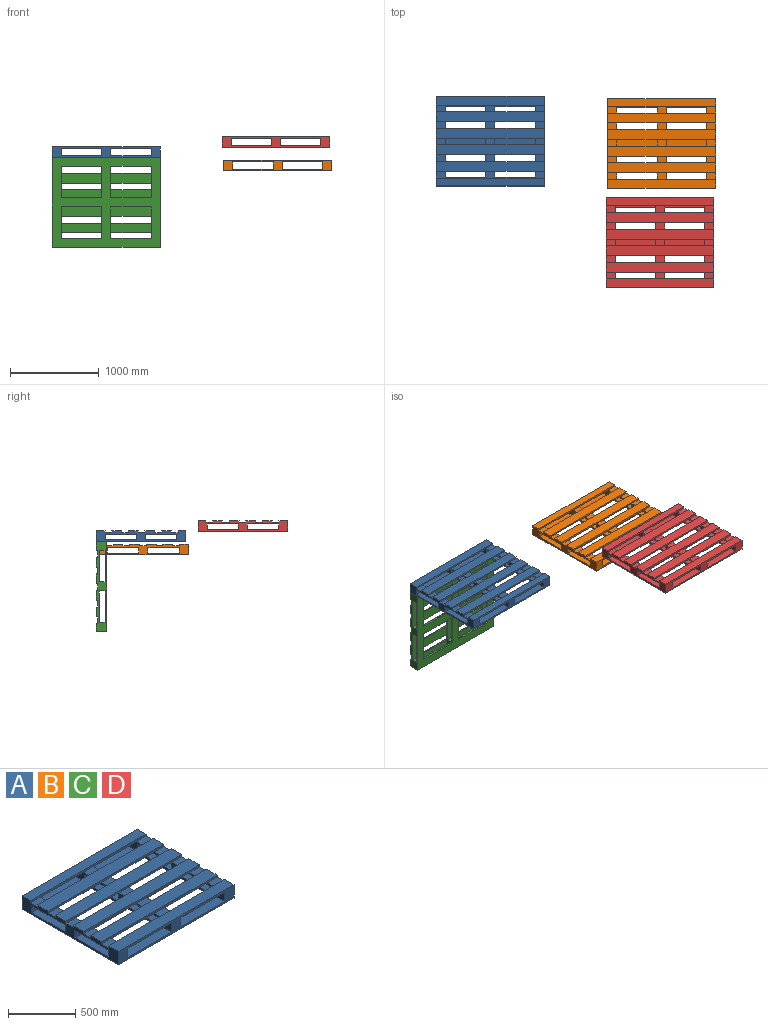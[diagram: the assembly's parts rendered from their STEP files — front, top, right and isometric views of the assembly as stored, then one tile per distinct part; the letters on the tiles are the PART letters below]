
ASSEMBLY  parts=4 mates=1
PART A: 98 faces, bbox 1219.2x1016x120.7 mm
  f0: plane 457.2x111.25mm, normal (0,0,-1), area 50864.4mm2, adj f36,f37,f88,f97
  f1: plane 457.2x111.25mm, normal (0,0,-1), area 50864.4mm2, adj f36,f37,f83,f92
  f2: plane 457.2x88.39mm, normal (0,0,-1), area 40412.8mm2, adj f23,f36,f37,f87
  f3: plane 457.2x111.25mm, normal (0,0,-1), area 50864.4mm2, adj f36,f37,f73,f78
  f4: plane 457.2x111.25mm, normal (0,0,-1), area 50864.4mm2, adj f36,f37,f77,f93
  f5: plane 457.2x111.25mm, normal (0,0,-1), area 50864.4mm2, adj f38,f40,f88,f97
  f6: plane 457.2x111.25mm, normal (0,0,-1), area 50864.4mm2, adj f38,f40,f83,f92
  f7: plane 457.2x88.39mm, normal (0,0,-1), area 40412.8mm2, adj f23,f38,f40,f87
  f8: plane 457.2x111.25mm, normal (0,0,-1), area 50864.4mm2, adj f38,f40,f73,f78
  f9: plane 457.2x111.25mm, normal (0,0,-1), area 50864.4mm2, adj f38,f40,f77,f93
  f10: plane 1219.2x111.25mm, normal (0,0,1), area 135638.4mm2, adj f15,f16,f88,f97
  f11: plane 1219.2x111.25mm, normal (0,0,1), area 135638.4mm2, adj f15,f16,f83,f92
  f12: plane 1219.2x88.39mm, normal (0,0,1), area 107767.5mm2, adj f15,f16,f23,f87
  f13: plane 1219.2x111.25mm, normal (0,0,1), area 135638.4mm2, adj f15,f16,f73,f78
  f14: plane 1219.2x111.25mm, normal (0,0,1), area 135638.4mm2, adj f15,f16,f77,f93
  f15: plane 1016x120.65mm, normal (1,0,0), area 70161.2mm2, adj f10,f11,f12,f13,f14,f17,f20,f23
  f16: plane 1016x120.65mm, normal (-1,0,0), area 70161.2mm2, adj f10,f11,f12,f13,f14,f17,f21,f22
  f17: plane 1219.2x120.65mm, normal (0,-1,0), area 71612.8mm2, adj f15,f16,f24,f27,f34,f36,f37,f38
  f18: plane 355.6x101.6mm, normal (0,0,-1), area 36129mm2, adj f36,f38,f48,f49
  f19: plane 355.6x101.6mm, normal (0,0,-1), area 36129mm2, adj f36,f38,f46,f47
  f20: plane 355.6x101.6mm, normal (0,0,-1), area 36129mm2, adj f15,f40,f44,f45
  f21: plane 355.6x101.6mm, normal (0,0,-1), area 36129mm2, adj f16,f37,f52,f53
  f22: plane 355.6x101.6mm, normal (0,0,-1), area 36129mm2, adj f16,f37,f50,f51
  f23: plane 1219.2x120.65mm, normal (0,1,0), area 71612.8mm2, adj f2,f7,f12,f15,f16,f24,f29,f33
  f24: plane 1219.2x1016mm, normal (0,0,-1), area 588385.9mm2, adj f15,f16,f17,f23,f54,f55,f56,f57
  f25: plane 457.2x101.6mm, normal (0,0,1), area 46451.5mm2, adj f38,f40,f59,f66
  f26: plane 355.6x101.6mm, normal (0,0,1), area 36129mm2, adj f15,f42,f43,f67
  f27: plane 457.2x101.6mm, normal (0,0,1), area 46451.5mm2, adj f17,f38,f40,f68
  f28: plane 355.6x101.6mm, normal (0,0,1), area 36129mm2, adj f16,f52,f53,f62
  f29: plane 457.2x101.6mm, normal (0,0,1), area 46451.5mm2, adj f23,f36,f37,f63
  f30: plane 457.2x101.6mm, normal (0,0,1), area 46451.5mm2, adj f36,f37,f56,f65
  f31: plane 355.6x101.6mm, normal (0,0,1), area 36129mm2, adj f15,f44,f45,f58
  f32: plane 355.6x101.6mm, normal (0,0,1), area 36129mm2, adj f48,f49,f60,f64
  f33: plane 457.2x101.6mm, normal (0,0,1), area 46451.5mm2, adj f23,f38,f40,f61
  f34: plane 457.2x101.6mm, normal (0,0,1), area 46451.5mm2, adj f17,f36,f37,f54
  f35: plane 355.6x101.6mm, normal (0,0,1), area 36129mm2, adj f16,f50,f51,f55
  f36: plane 1016x82.55mm, normal (-1,0,0), area 38709.6mm2, adj f0,f1,f2,f3,f4,f17,f18,f19
  f37: plane 1016x82.55mm, normal (1,0,0), area 38709.6mm2, adj f0,f1,f2,f3,f4,f17,f21,f22
  f38: plane 1016x82.55mm, normal (1,0,0), area 38709.6mm2, adj f5,f6,f7,f8,f9,f17,f18,f19
  f39: plane 355.6x101.6mm, normal (0,0,1), area 36129mm2, adj f46,f47,f57,f69
  f40: plane 1016x82.55mm, normal (-1,0,0), area 38709.6mm2, adj f5,f6,f7,f8,f9,f17,f20,f23
  f41: plane 355.6x101.6mm, normal (0,0,-1), area 36129mm2, adj f15,f40,f42,f43
  f42: plane 101.6x63.5mm, normal (0,1,0), area 6451.6mm2, adj f15,f26,f40,f41
  f43: plane 101.6x63.5mm, normal (0,-1,0), area 6451.6mm2, adj f15,f26,f40,f41
  f44: plane 101.6x63.5mm, normal (0,1,0), area 6451.6mm2, adj f15,f20,f31,f40
  f45: plane 101.6x63.5mm, normal (0,-1,0), area 6451.6mm2, adj f15,f20,f31,f40
  f46: plane 101.6x63.5mm, normal (0,1,0), area 6451.6mm2, adj f19,f36,f38,f39
  f47: plane 101.6x63.5mm, normal (0,-1,0), area 6451.6mm2, adj f19,f36,f38,f39
  f48: plane 101.6x63.5mm, normal (0,1,0), area 6451.6mm2, adj f18,f32,f36,f38
  f49: plane 101.6x63.5mm, normal (0,-1,0), area 6451.6mm2, adj f18,f32,f36,f38
  f50: plane 101.6x63.5mm, normal (0,1,0), area 6451.6mm2, adj f16,f22,f35,f37
  f51: plane 101.6x63.5mm, normal (0,-1,0), area 6451.6mm2, adj f16,f22,f35,f37
  f52: plane 101.6x63.5mm, normal (0,-1,0), area 6451.6mm2, adj f16,f21,f28,f37
  f53: plane 101.6x63.5mm, normal (0,1,0), area 6451.6mm2, adj f16,f21,f28,f37
  f54: plane 457.2x19.05mm, normal (0,1,0), area 8709.7mm2, adj f24,f34,f55,f57
  f55: plane 355.6x19.05mm, normal (1,0,0), area 6774.2mm2, adj f24,f35,f54,f56
  f56: plane 457.2x19.05mm, normal (0,-1,0), area 8709.7mm2, adj f24,f30,f55,f57
  f57: plane 355.6x19.05mm, normal (-1,0,0), area 6774.2mm2, adj f24,f39,f54,f56
  f58: plane 355.6x19.05mm, normal (-1,0,0), area 6774.2mm2, adj f24,f31,f59,f61
  f59: plane 457.2x19.05mm, normal (0,1,0), area 8709.7mm2, adj f24,f25,f58,f60
  f60: plane 355.6x19.05mm, normal (1,0,0), area 6774.2mm2, adj f24,f32,f59,f61
  f61: plane 457.2x19.05mm, normal (0,-1,0), area 8709.7mm2, adj f24,f33,f58,f60
  f62: plane 355.6x19.05mm, normal (1,0,0), area 6774.2mm2, adj f24,f28,f63,f65
  f63: plane 457.2x19.05mm, normal (0,-1,0), area 8709.7mm2, adj f24,f29,f62,f64
  f64: plane 355.6x19.05mm, normal (-1,0,0), area 6774.2mm2, adj f24,f32,f63,f65
  f65: plane 457.2x19.05mm, normal (0,1,0), area 8709.7mm2, adj f24,f30,f62,f64
  f66: plane 457.2x19.05mm, normal (0,-1,0), area 8709.7mm2, adj f24,f25,f67,f69
  f67: plane 355.6x19.05mm, normal (-1,0,0), area 6774.2mm2, adj f24,f26,f66,f68
  f68: plane 457.2x19.05mm, normal (0,1,0), area 8709.7mm2, adj f24,f27,f67,f69
  f69: plane 355.6x19.05mm, normal (1,0,0), area 6774.2mm2, adj f24,f39,f66,f68
  f70: plane 457.2x101.6mm, normal (0,0,-1), area 46451.5mm2, adj f17,f36,f37,f79
  f71: plane 457.2x101.6mm, normal (0,0,-1), area 46451.5mm2, adj f17,f38,f40,f79
  f72: plane 1219.2x101.6mm, normal (0,0,1), area 123870.7mm2, adj f15,f16,f17,f79
  f73: plane 1219.2x19.05mm, normal (0,1,0), area 23225.8mm2, adj f3,f8,f13,f15,f16,f74,f75,f76
  f74: plane 101.6x76.2mm, normal (0,0,1), area 7741.9mm2, adj f16,f37,f73,f77
  f75: plane 101.6x76.2mm, normal (0,0,1), area 7741.9mm2, adj f36,f38,f73,f77
  f76: plane 101.6x76.2mm, normal (0,0,1), area 7741.9mm2, adj f15,f40,f73,f77
  f77: plane 1219.2x19.05mm, normal (0,-1,0), area 23225.8mm2, adj f4,f9,f14,f15,f16,f74,f75,f76
  f78: plane 1219.2x19.05mm, normal (0,-1,0), area 23225.8mm2, adj f3,f8,f13,f15,f16,f80,f81,f82
  f79: plane 1219.2x19.05mm, normal (0,1,0), area 23225.8mm2, adj f15,f16,f70,f71,f72,f80,f81,f82
  f80: plane 101.6x76.2mm, normal (0,0,1), area 7741.9mm2, adj f16,f37,f78,f79
  f81: plane 101.6x76.2mm, normal (0,0,1), area 7741.9mm2, adj f36,f38,f78,f79
  f82: plane 101.6x76.2mm, normal (0,0,1), area 7741.9mm2, adj f15,f40,f78,f79
  f83: plane 1219.2x19.05mm, normal (0,1,0), area 23225.8mm2, adj f1,f6,f11,f15,f16,f84,f85,f86
  f84: plane 101.6x76.2mm, normal (0,0,1), area 7741.9mm2, adj f16,f37,f83,f87
  f85: plane 101.6x76.2mm, normal (0,0,1), area 7741.9mm2, adj f36,f38,f83,f87
  f86: plane 101.6x76.2mm, normal (0,0,1), area 7741.9mm2, adj f15,f40,f83,f87
  f87: plane 1219.2x19.05mm, normal (0,-1,0), area 23225.8mm2, adj f2,f7,f12,f15,f16,f84,f85,f86
  f88: plane 1219.2x19.05mm, normal (0,1,0), area 23225.8mm2, adj f0,f5,f10,f15,f16,f89,f90,f91
  f89: plane 101.6x76.2mm, normal (0,0,1), area 7741.9mm2, adj f16,f37,f88,f92
  f90: plane 101.6x76.2mm, normal (0,0,1), area 7741.9mm2, adj f36,f38,f88,f92
  f91: plane 101.6x76.2mm, normal (0,0,1), area 7741.9mm2, adj f15,f40,f88,f92
  f92: plane 1219.2x19.05mm, normal (0,-1,0), area 23225.8mm2, adj f1,f6,f11,f15,f16,f89,f90,f91
  f93: plane 1219.2x19.05mm, normal (0,1,0), area 23225.8mm2, adj f4,f9,f14,f15,f16,f94,f95,f96
  f94: plane 101.6x76.2mm, normal (0,0,1), area 7741.9mm2, adj f16,f37,f93,f97
  f95: plane 101.6x76.2mm, normal (0,0,1), area 7741.9mm2, adj f36,f38,f93,f97
  f96: plane 101.6x76.2mm, normal (0,0,1), area 7741.9mm2, adj f15,f40,f93,f97
  f97: plane 1219.2x19.05mm, normal (0,-1,0), area 23225.8mm2, adj f0,f5,f10,f15,f16,f94,f95,f96
PART B: same geometry as A
PART C: same geometry as A
PART D: same geometry as A
PLACE A rot(axis=(0,0,1),180deg) t=(77.65,-720.15,97.72)mm
PLACE B t=(2012.25,-747.99,-53.87)mm
PLACE C rot(axis=(-1,0,0),90deg) t=(77.65,-282,-461.08)mm
PLACE D t=(1993.95,-1872.01,213.79)mm
MATE fastened A.f24 <-> C.f17  axis (0,0,1) through (77.65,-212.15,46.92)mm
